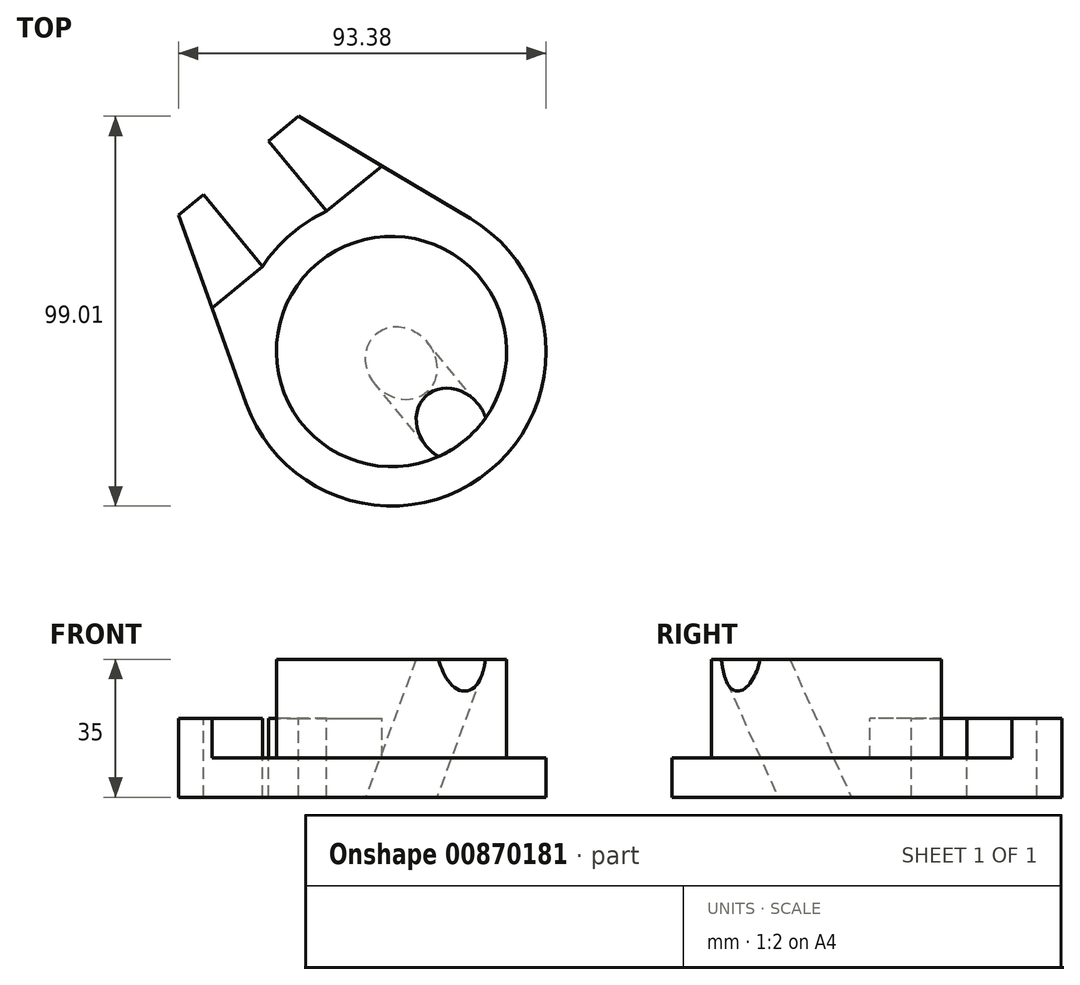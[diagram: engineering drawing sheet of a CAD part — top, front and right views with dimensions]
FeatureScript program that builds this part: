
annotation { "Feature Type Name" : "Feature", "Feature Type Description" : "" }
export const myFeature = defineFeature(function(context is Context, id is Id, definition is map)
    precondition{}
    {
        {
            var Q0;
            Q0=qCreatedBy(makeId("Top.planeOp"),FACE);
            var sketch = newSketch(context, id + "F0", { "sketchPlane" : qUnion([Q0])});
            skCircle(sketch, "E0", {"center": v(0, 0) * mm, "radius": 29.25 * mm});
            skSolve(sketch);
        }
        {
            var Q0;
            Q0 = qSketchRegion(id + "F0", true);
            extrude(context, id + "F1", {"entities" : qUnion([Q0]), "depth" : 25 * mm, "offsetDistance" : 25 * mm});
        }
        {
            var Q0;
            Q0=makeQuery(id+"F1.opExtrude","CAP_FACE",FACE,{"disambiguationData":[OSD([sQuery(id+"F0.wireOp",EDGE,"E0")])],"isStart":false});
            var sketch = newSketch(context, id + "F2", { "sketchPlane" : qUnion([Q0])});
            skArc(sketch, "E1", {"start": v(11.56, 37.5) * mm, "mid": v(0.85, 39.24) * mm, "end": v(-9.94, 37.97) * mm});
            skLineSegment(sketch, "E2.top", {"start": v(19.76, 61.14) * mm, "end": v(11.56, 61.14) * mm});
            skLineSegment(sketch, "E3.left", {"start": v(11.56, 37.5) * mm, "end": v(11.56, 61.14) * mm});
            skLineSegment(sketch, "E3.right", {"start": v(-9.94, 37.97) * mm, "end": v(-9.94, 61.14) * mm});
            skPoint(sketch, "E3.middle", {"position": v(0, 39.25) * mm});
            skPoint(sketch, "E3.top.end.orphan", {"position": v(-9.94, 75.5) * mm});
            skPoint(sketch, "E4.orphan", {"position": v(11.56, 75.5) * mm});
            skLineSegment(sketch, "E5.trimOffspring", {"start": v(-9.94, 61.14) * mm, "end": v(-19.76, 61.14) * mm});
            skLineSegment(sketch, "E6", {"start": v(-19.76, 61.14) * mm, "end": v(-36.94, 13.25) * mm});
            skLineSegment(sketch, "E7", {"start": v(19.76, 61.14) * mm, "end": v(36.94, 13.25) * mm});
            skArc(sketch, "E8.trimOffspring", {"start": v(-36.94, 13.25) * mm, "mid": v(0, -39.25) * mm, "end": v(36.94, 13.25) * mm});
            skLineSegment(sketch, "E9", {"start": v(-9.94, 37.97) * mm, "end": v(-28.08, 37.97) * mm});
            skLineSegment(sketch, "E10", {"start": v(11.56, 37.5) * mm, "end": v(28.24, 37.5) * mm});
            skSolve(sketch);
        }
        {
            var Q0;
            Q0=makeQuery(id+"F2.imprint","IMPRINT",FACE,{"disambiguationData":[TD([[makeQuery(id+"F2.imprint","IMPRINT",EDGE,{"derivedFrom":sQuery(id+"F2.wireOp",EDGE,"E1")}),1.0]])]});
            var Q1;
            Q1=makeQuery(id+"F2.imprint","IMPRINT",FACE,{"disambiguationData":[TD([[makeQuery(id+"F2.imprint","IMPRINT",EDGE,{"derivedFrom":makeQuery(id+"F1.opExtrude","CAP_EDGE",EDGE,{"disambiguationData":[OSD([sQuery(id+"F0.wireOp",EDGE,"E0")])],"isStart":false})}),1.0]])]});
            extrude(context, id + "F3", {"entities" : qUnion([Q0, Q1]), "operationType" : NewBodyOperationType.ADD, "depth" : 10 * mm, "offsetDistance" : 25 * mm});
        }
        {
            var Q0;
            {var subQ0=sQuery(id+"F2.wireOp",EDGE,"E2.top");Q0=makeQuery(id+"F2.imprint","IMPRINT",FACE,{"disambiguationData":[TD([[makeQuery(id+"F2.imprint","IMPRINT",EDGE,{"derivedFrom":subQ0}),1.0]])]});}
            var Q1;
            Q1=makeQuery(id+"F2.imprint","IMPRINT",FACE,{"disambiguationData":[TD([[makeQuery(id+"F2.imprint","IMPRINT",EDGE,{"derivedFrom":sQuery(id+"F2.wireOp",EDGE,"E3.right")}),1.0]])]});
            extrude(context, id + "F4", {"entities" : qUnion([Q0, Q1]), "operationType" : NewBodyOperationType.ADD, "endBound" : BoundingType.SYMMETRIC, "depth" : 20 * mm, "offsetDistance" : 25 * mm});
        }
        {
            var Q0;
            Q0=qCreatedBy(makeId("Right.planeOp"),FACE);
            var sketch = newSketch(context, id + "F5", { "sketchPlane" : qUnion([Q0])});
            skLineSegment(sketch, "E11", {"start": v(17.15, 68.36) * mm, "end": v(-36.68, -36.3) * mm, "construction": true});
            skSolve(sketch);
        }
        {
            var Q0;
            Q0=sQuery(id+"F5.wireOp",EDGE,"E11");
            cPlane(context, id + "F6", {"entities" : qUnion([Q0]), "cplaneType" : CPlaneType.LINE_ANGLE, "offset" : 25 * mm, "angle" : 90 * degree, "width" : 150 * mm, "height" : 150 * mm});
        }
        {
            var Q0;
            Q0=qCreatedBy(id+"F6.planeOp",FACE);
            var sketch = newSketch(context, id + "F7", { "sketchPlane" : qUnion([Q0])});
            skLineSegment(sketch, "E12", {"start": v(0, 69.86) * mm, "end": v(-15.02, 69.86) * mm, "construction": true});
            skLineSegment(sketch, "E13", {"start": v(-114.65, 17.88) * mm, "end": v(-110.08, 36.02) * mm, "construction": true});
            skSolve(sketch);
        }
        {
            var Q0;
            Q0=sQuery(id+"F7.wireOp",EDGE,"E12");
            cPlane(context, id + "F8", {"entities" : qUnion([Q0]), "cplaneType" : CPlaneType.LINE_ANGLE, "offset" : 25 * mm, "angle" : 60 * degree, "width" : 150 * mm, "height" : 150 * mm});
        }
        {
            var Q0;
            Q0=qCreatedBy(id+"F8.planeOp",FACE);
            var sketch = newSketch(context, id + "F9", { "sketchPlane" : qUnion([Q0])});
            skCircle(sketch, "E14", {"center": v(0, -20.86) * mm, "radius": 8.5 * mm});
            skSolve(sketch);
        }
        {
            var Q0;
            Q0=makeQuery(id+"F9.imprint","IMPRINT",FACE,{"disambiguationData":[TD([[makeQuery(id+"F9.imprint","IMPRINT",EDGE,{"derivedFrom":sQuery(id+"F9.wireOp",EDGE,"E14")}),1.0]])]});
            extrude(context, id + "F10", {"entities" : qUnion([Q0]), "operationType" : NewBodyOperationType.REMOVE, "oppositeDirection" : true, "depth" : 152 * mm, "offsetDistance" : 25 * mm});
        }
        {
            var Q0;
            Q0=makeQuery(id+"F1.opExtrude","SWEPT_BODY",BODY,{"disambiguationData":[OSD([sQuery(id+"F0.wireOp",EDGE,"E0")])]});
            var Q1;
            Q1=makeQuery(id+"F4.opExtrude","CAP_EDGE",EDGE,{"disambiguationData":[OSD([sQuery(id+"F2.wireOp",EDGE,"E7")])],"isStart":true});
            transform(context, id + "F11", {"entities" : qUnion([Q0]), "transformType" : TransformType.ROTATION, "transformAxis" : qUnion([Q1]), "angle" : 180 * degree, "makeCopy" : false});
        }
    });
